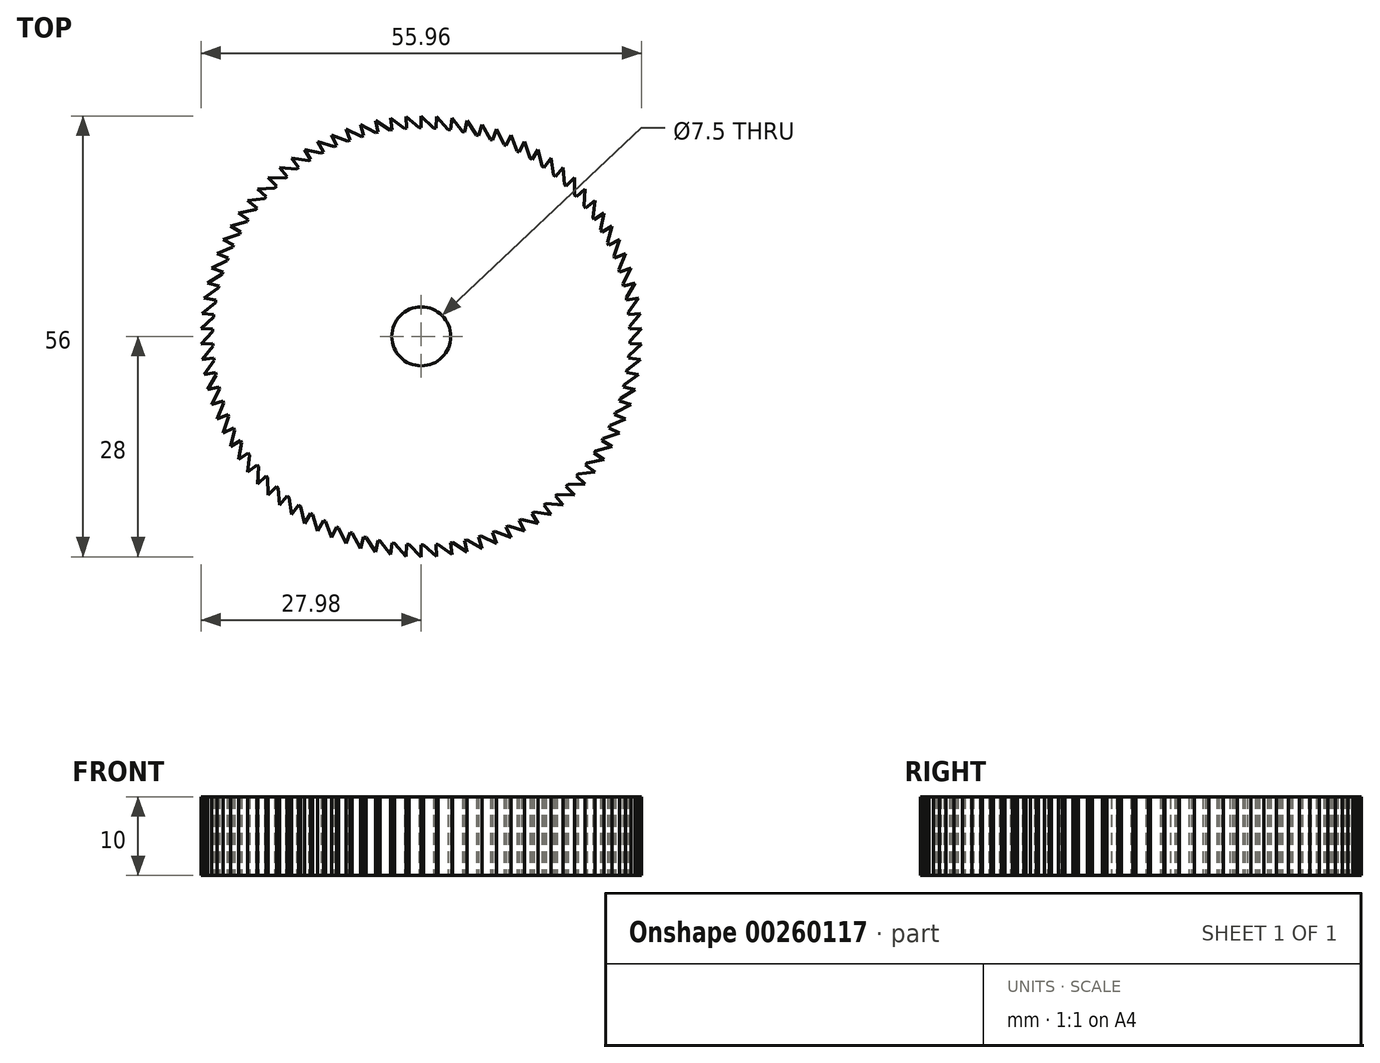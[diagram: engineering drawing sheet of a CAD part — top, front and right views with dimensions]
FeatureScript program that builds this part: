
annotation { "Feature Type Name" : "Feature", "Feature Type Description" : "" }
export const myFeature = defineFeature(function(context is Context, id is Id, definition is map)
    precondition{}
    {
        {
            var Q0;
            Q0=qCreatedBy(makeId("Top.planeOp"),FACE);
            var sketch = newSketch(context, id + "F0", { "sketchPlane" : qUnion([Q0])});
            skArc(sketch, "E0", {"start": v(25.78, -6.12) * mm, "mid": v(26.12, -4.45) * mm, "end": v(26.35, -2.77) * mm, "construction": true});
            skCircle(sketch, "E1", {"center": v(0, 0) * mm, "radius": 3.75 * mm});
            skLineSegment(sketch, "E2", {"start": v(0, 26.5) * mm, "end": v(0, 28) * mm});
            skLineSegment(sketch, "E3", {"start": v(0, 28) * mm, "end": v(1.55, 26.45) * mm});
            skLineSegment(sketch, "E4.anchor1", {"start": v(0, 0) * mm, "end": v(0, 26.5) * mm, "construction": true});
            skLineSegment(sketch, "E4.anchor2", {"start": v(0, 0) * mm, "end": v(0, 26.5) * mm, "construction": true});
            skLineSegment(sketch, "E5.1.0", {"start": v(-1.95, 27.93) * mm, "end": v(-0.3, 26.5) * mm});
            skLineSegment(sketch, "E5.1.1", {"start": v(-1.85, 26.44) * mm, "end": v(-1.95, 27.93) * mm});
            skLineSegment(sketch, "E5.2.0", {"start": v(-3.9, 27.73) * mm, "end": v(-2.15, 26.41) * mm});
            skLineSegment(sketch, "E5.2.1", {"start": v(-3.69, 26.24) * mm, "end": v(-3.9, 27.73) * mm});
            skLineSegment(sketch, "E5.3.0", {"start": v(-5.82, 27.39) * mm, "end": v(-3.99, 26.2) * mm});
            skLineSegment(sketch, "E5.3.1", {"start": v(-5.5, 25.92) * mm, "end": v(-5.82, 27.39) * mm});
            skLineSegment(sketch, "E5.4.0", {"start": v(-7.72, 26.92) * mm, "end": v(-5.8, 25.86) * mm});
            skLineSegment(sketch, "E5.4.1", {"start": v(-7.3, 25.47) * mm, "end": v(-7.72, 26.92) * mm});
            skLineSegment(sketch, "E5.5.0", {"start": v(-9.58, 26.31) * mm, "end": v(-7.6, 25.39) * mm});
            skLineSegment(sketch, "E5.5.1", {"start": v(-9.06, 24.9) * mm, "end": v(-9.58, 26.31) * mm});
            skLineSegment(sketch, "E5.6.0", {"start": v(-11.39, 25.58) * mm, "end": v(-9.35, 24.8) * mm});
            skLineSegment(sketch, "E5.6.1", {"start": v(-10.78, 24.2) * mm, "end": v(-11.39, 25.58) * mm});
            skLineSegment(sketch, "E5.7.0", {"start": v(-13.15, 24.72) * mm, "end": v(-11.06, 24.08) * mm});
            skLineSegment(sketch, "E5.7.1", {"start": v(-12.44, 23.4) * mm, "end": v(-13.15, 24.72) * mm});
            skLineSegment(sketch, "E5.8.0", {"start": v(-14.84, 23.75) * mm, "end": v(-12.7, 23.25) * mm});
            skLineSegment(sketch, "E5.8.1", {"start": v(-14.04, 22.47) * mm, "end": v(-14.84, 23.75) * mm});
            skLineSegment(sketch, "E5.9.0", {"start": v(-16.46, 22.65) * mm, "end": v(-14.3, 22.31) * mm});
            skLineSegment(sketch, "E5.9.1", {"start": v(-15.58, 21.44) * mm, "end": v(-16.46, 22.65) * mm});
            skLineSegment(sketch, "E5.10.0", {"start": v(-18, 21.45) * mm, "end": v(-15.82, 21.26) * mm});
            skLineSegment(sketch, "E5.10.1", {"start": v(-17.03, 20.3) * mm, "end": v(-18, 21.45) * mm});
            skLineSegment(sketch, "E5.11.0", {"start": v(-19.45, 20.14) * mm, "end": v(-17.27, 20.1) * mm});
            skLineSegment(sketch, "E5.11.1", {"start": v(-18.4, 19.06) * mm, "end": v(-19.45, 20.14) * mm});
            skLineSegment(sketch, "E5.12.0", {"start": v(-20.8, 18.74) * mm, "end": v(-18.63, 18.85) * mm});
            skLineSegment(sketch, "E5.12.1", {"start": v(-19.7, 17.73) * mm, "end": v(-20.8, 18.74) * mm});
            skLineSegment(sketch, "E5.13.0", {"start": v(-22.06, 17.24) * mm, "end": v(-19.9, 17.5) * mm});
            skLineSegment(sketch, "E5.13.1", {"start": v(-20.88, 16.32) * mm, "end": v(-22.06, 17.24) * mm});
            skLineSegment(sketch, "E5.14.0", {"start": v(-23.21, 15.66) * mm, "end": v(-21.07, 16.07) * mm});
            skLineSegment(sketch, "E5.14.1", {"start": v(-21.97, 14.82) * mm, "end": v(-23.21, 15.66) * mm});
            skLineSegment(sketch, "E5.15.0", {"start": v(-24.25, 14) * mm, "end": v(-22.14, 14.57) * mm});
            skLineSegment(sketch, "E5.15.1", {"start": v(-22.95, 13.25) * mm, "end": v(-24.25, 14) * mm});
            skLineSegment(sketch, "E5.16.0", {"start": v(-25.17, 12.27) * mm, "end": v(-23.1, 12.99) * mm});
            skLineSegment(sketch, "E5.16.1", {"start": v(-23.82, 11.62) * mm, "end": v(-25.17, 12.27) * mm});
            skLineSegment(sketch, "E5.17.0", {"start": v(-25.96, 10.49) * mm, "end": v(-23.95, 11.34) * mm});
            skLineSegment(sketch, "E5.17.1", {"start": v(-24.57, 9.93) * mm, "end": v(-25.96, 10.49) * mm});
            skLineSegment(sketch, "E5.18.0", {"start": v(-26.63, 8.65) * mm, "end": v(-24.68, 9.64) * mm});
            skLineSegment(sketch, "E5.18.1", {"start": v(-25.2, 8.19) * mm, "end": v(-26.63, 8.65) * mm});
            skLineSegment(sketch, "E5.19.0", {"start": v(-27.17, 6.77) * mm, "end": v(-25.3, 7.9) * mm});
            skLineSegment(sketch, "E5.19.1", {"start": v(-25.71, 6.41) * mm, "end": v(-27.17, 6.77) * mm});
            skLineSegment(sketch, "E5.20.0", {"start": v(-27.57, 4.86) * mm, "end": v(-25.78, 6.12) * mm});
            skLineSegment(sketch, "E5.20.1", {"start": v(-26.1, 4.6) * mm, "end": v(-27.57, 4.86) * mm});
            skLineSegment(sketch, "E5.21.0", {"start": v(-27.85, 2.93) * mm, "end": v(-26.15, 4.3) * mm});
            skLineSegment(sketch, "E5.21.1", {"start": v(-26.35, 2.77) * mm, "end": v(-27.85, 2.93) * mm});
            skLineSegment(sketch, "E5.22.0", {"start": v(-27.98, 0.98) * mm, "end": v(-26.38, 2.47) * mm});
            skLineSegment(sketch, "E5.22.1", {"start": v(-26.48, 0.92) * mm, "end": v(-27.98, 0.98) * mm});
            skLineSegment(sketch, "E5.23.0", {"start": v(-27.98, -0.98) * mm, "end": v(-26.5, 0.62) * mm});
            skLineSegment(sketch, "E5.23.1", {"start": v(-26.48, -0.92) * mm, "end": v(-27.98, -0.98) * mm});
            skLineSegment(sketch, "E5.24.0", {"start": v(-27.85, -2.93) * mm, "end": v(-26.47, -1.23) * mm});
            skLineSegment(sketch, "E5.24.1", {"start": v(-26.35, -2.77) * mm, "end": v(-27.85, -2.93) * mm});
            skLineSegment(sketch, "E5.25.0", {"start": v(-27.57, -4.86) * mm, "end": v(-26.32, -3.07) * mm});
            skLineSegment(sketch, "E5.25.1", {"start": v(-26.1, -4.6) * mm, "end": v(-27.57, -4.86) * mm});
            skLineSegment(sketch, "E5.26.0", {"start": v(-27.17, -6.77) * mm, "end": v(-26.04, -4.9) * mm});
            skLineSegment(sketch, "E5.26.1", {"start": v(-25.71, -6.41) * mm, "end": v(-27.17, -6.77) * mm});
            skLineSegment(sketch, "E5.27.0", {"start": v(-26.63, -8.65) * mm, "end": v(-25.64, -6.7) * mm});
            skLineSegment(sketch, "E5.27.1", {"start": v(-25.2, -8.19) * mm, "end": v(-26.63, -8.65) * mm});
            skLineSegment(sketch, "E5.28.0", {"start": v(-25.96, -10.49) * mm, "end": v(-25.1, -8.48) * mm});
            skLineSegment(sketch, "E5.28.1", {"start": v(-24.57, -9.93) * mm, "end": v(-25.96, -10.49) * mm});
            skLineSegment(sketch, "E5.29.0", {"start": v(-25.17, -12.27) * mm, "end": v(-24.45, -10.2) * mm});
            skLineSegment(sketch, "E5.29.1", {"start": v(-23.82, -11.62) * mm, "end": v(-25.17, -12.27) * mm});
            skLineSegment(sketch, "E5.30.0", {"start": v(-24.25, -14) * mm, "end": v(-23.68, -11.89) * mm});
            skLineSegment(sketch, "E5.30.1", {"start": v(-22.95, -13.25) * mm, "end": v(-24.25, -14) * mm});
            skLineSegment(sketch, "E5.31.0", {"start": v(-23.21, -15.66) * mm, "end": v(-22.8, -13.51) * mm});
            skLineSegment(sketch, "E5.31.1", {"start": v(-21.97, -14.82) * mm, "end": v(-23.21, -15.66) * mm});
            skLineSegment(sketch, "E5.32.0", {"start": v(-22.06, -17.24) * mm, "end": v(-21.8, -15.07) * mm});
            skLineSegment(sketch, "E5.32.1", {"start": v(-20.88, -16.32) * mm, "end": v(-22.06, -17.24) * mm});
            skLineSegment(sketch, "E5.33.0", {"start": v(-20.8, -18.74) * mm, "end": v(-20.7, -16.55) * mm});
            skLineSegment(sketch, "E5.33.1", {"start": v(-19.7, -17.73) * mm, "end": v(-20.8, -18.74) * mm});
            skLineSegment(sketch, "E5.34.0", {"start": v(-19.45, -20.14) * mm, "end": v(-19.49, -17.96) * mm});
            skLineSegment(sketch, "E5.34.1", {"start": v(-18.4, -19.06) * mm, "end": v(-19.45, -20.14) * mm});
            skLineSegment(sketch, "E5.35.0", {"start": v(-18, -21.45) * mm, "end": v(-18.19, -19.27) * mm});
            skLineSegment(sketch, "E5.35.1", {"start": v(-17.03, -20.3) * mm, "end": v(-18, -21.45) * mm});
            skLineSegment(sketch, "E5.36.0", {"start": v(-16.46, -22.65) * mm, "end": v(-16.8, -20.5) * mm});
            skLineSegment(sketch, "E5.36.1", {"start": v(-15.58, -21.44) * mm, "end": v(-16.46, -22.65) * mm});
            skLineSegment(sketch, "E5.37.0", {"start": v(-14.84, -23.75) * mm, "end": v(-15.33, -21.62) * mm});
            skLineSegment(sketch, "E5.37.1", {"start": v(-14.04, -22.47) * mm, "end": v(-14.84, -23.75) * mm});
            skLineSegment(sketch, "E5.38.0", {"start": v(-13.15, -24.72) * mm, "end": v(-13.78, -22.63) * mm});
            skLineSegment(sketch, "E5.38.1", {"start": v(-12.44, -23.4) * mm, "end": v(-13.15, -24.72) * mm});
            skLineSegment(sketch, "E5.39.0", {"start": v(-11.39, -25.58) * mm, "end": v(-12.17, -23.54) * mm});
            skLineSegment(sketch, "E5.39.1", {"start": v(-10.78, -24.2) * mm, "end": v(-11.39, -25.58) * mm});
            skLineSegment(sketch, "E5.40.0", {"start": v(-9.58, -26.31) * mm, "end": v(-10.5, -24.33) * mm});
            skLineSegment(sketch, "E5.40.1", {"start": v(-9.06, -24.9) * mm, "end": v(-9.58, -26.31) * mm});
            skLineSegment(sketch, "E5.41.0", {"start": v(-7.72, -26.92) * mm, "end": v(-8.78, -25) * mm});
            skLineSegment(sketch, "E5.41.1", {"start": v(-7.3, -25.47) * mm, "end": v(-7.72, -26.92) * mm});
            skLineSegment(sketch, "E5.42.0", {"start": v(-5.82, -27.39) * mm, "end": v(-7.01, -25.56) * mm});
            skLineSegment(sketch, "E5.42.1", {"start": v(-5.5, -25.92) * mm, "end": v(-5.82, -27.39) * mm});
            skLineSegment(sketch, "E5.43.0", {"start": v(-3.9, -27.73) * mm, "end": v(-5.21, -25.98) * mm});
            skLineSegment(sketch, "E5.43.1", {"start": v(-3.69, -26.24) * mm, "end": v(-3.9, -27.73) * mm});
            skLineSegment(sketch, "E5.44.0", {"start": v(-1.95, -27.93) * mm, "end": v(-3.39, -26.28) * mm});
            skLineSegment(sketch, "E5.44.1", {"start": v(-1.85, -26.44) * mm, "end": v(-1.95, -27.93) * mm});
            skLineSegment(sketch, "E5.45.0", {"start": v(0, -28) * mm, "end": v(-1.55, -26.45) * mm});
            skLineSegment(sketch, "E5.45.1", {"start": v(0, -26.5) * mm, "end": v(0, -28) * mm});
            skLineSegment(sketch, "E5.46.0", {"start": v(1.95, -27.93) * mm, "end": v(0.3, -26.5) * mm});
            skLineSegment(sketch, "E5.46.1", {"start": v(1.85, -26.44) * mm, "end": v(1.95, -27.93) * mm});
            skLineSegment(sketch, "E5.47.0", {"start": v(3.9, -27.73) * mm, "end": v(2.15, -26.41) * mm});
            skLineSegment(sketch, "E5.47.1", {"start": v(3.69, -26.24) * mm, "end": v(3.9, -27.73) * mm});
            skLineSegment(sketch, "E5.48.0", {"start": v(5.82, -27.39) * mm, "end": v(3.99, -26.2) * mm});
            skLineSegment(sketch, "E5.48.1", {"start": v(5.5, -25.92) * mm, "end": v(5.82, -27.39) * mm});
            skLineSegment(sketch, "E5.49.0", {"start": v(7.72, -26.92) * mm, "end": v(5.8, -25.86) * mm});
            skLineSegment(sketch, "E5.49.1", {"start": v(7.3, -25.47) * mm, "end": v(7.72, -26.92) * mm});
            skLineSegment(sketch, "E5.50.0", {"start": v(9.58, -26.31) * mm, "end": v(7.6, -25.39) * mm});
            skLineSegment(sketch, "E5.50.1", {"start": v(9.06, -24.9) * mm, "end": v(9.58, -26.31) * mm});
            skLineSegment(sketch, "E5.51.0", {"start": v(11.39, -25.58) * mm, "end": v(9.35, -24.8) * mm});
            skLineSegment(sketch, "E5.51.1", {"start": v(10.78, -24.2) * mm, "end": v(11.39, -25.58) * mm});
            skLineSegment(sketch, "E5.52.0", {"start": v(13.15, -24.72) * mm, "end": v(11.06, -24.08) * mm});
            skLineSegment(sketch, "E5.52.1", {"start": v(12.44, -23.4) * mm, "end": v(13.15, -24.72) * mm});
            skLineSegment(sketch, "E5.53.0", {"start": v(14.84, -23.75) * mm, "end": v(12.7, -23.25) * mm});
            skLineSegment(sketch, "E5.53.1", {"start": v(14.04, -22.47) * mm, "end": v(14.84, -23.75) * mm});
            skLineSegment(sketch, "E5.54.0", {"start": v(16.46, -22.65) * mm, "end": v(14.3, -22.31) * mm});
            skLineSegment(sketch, "E5.54.1", {"start": v(15.58, -21.44) * mm, "end": v(16.46, -22.65) * mm});
            skLineSegment(sketch, "E5.55.0", {"start": v(18, -21.45) * mm, "end": v(15.82, -21.26) * mm});
            skLineSegment(sketch, "E5.55.1", {"start": v(17.03, -20.3) * mm, "end": v(18, -21.45) * mm});
            skLineSegment(sketch, "E5.56.0", {"start": v(19.45, -20.14) * mm, "end": v(17.27, -20.1) * mm});
            skLineSegment(sketch, "E5.56.1", {"start": v(18.4, -19.06) * mm, "end": v(19.45, -20.14) * mm});
            skLineSegment(sketch, "E5.57.0", {"start": v(20.8, -18.74) * mm, "end": v(18.63, -18.85) * mm});
            skLineSegment(sketch, "E5.57.1", {"start": v(19.7, -17.73) * mm, "end": v(20.8, -18.74) * mm});
            skLineSegment(sketch, "E5.58.0", {"start": v(22.06, -17.24) * mm, "end": v(19.9, -17.5) * mm});
            skLineSegment(sketch, "E5.58.1", {"start": v(20.88, -16.32) * mm, "end": v(22.06, -17.24) * mm});
            skLineSegment(sketch, "E5.59.0", {"start": v(23.21, -15.66) * mm, "end": v(21.07, -16.07) * mm});
            skLineSegment(sketch, "E5.59.1", {"start": v(21.97, -14.82) * mm, "end": v(23.21, -15.66) * mm});
            skLineSegment(sketch, "E5.60.0", {"start": v(24.25, -14) * mm, "end": v(22.14, -14.57) * mm});
            skLineSegment(sketch, "E5.60.1", {"start": v(22.95, -13.25) * mm, "end": v(24.25, -14) * mm});
            skLineSegment(sketch, "E5.61.0", {"start": v(25.17, -12.27) * mm, "end": v(23.1, -12.99) * mm});
            skLineSegment(sketch, "E5.61.1", {"start": v(23.82, -11.62) * mm, "end": v(25.17, -12.27) * mm});
            skLineSegment(sketch, "E5.62.0", {"start": v(25.96, -10.49) * mm, "end": v(23.95, -11.34) * mm});
            skLineSegment(sketch, "E5.62.1", {"start": v(24.57, -9.93) * mm, "end": v(25.96, -10.49) * mm});
            skLineSegment(sketch, "E5.63.0", {"start": v(26.63, -8.65) * mm, "end": v(24.68, -9.64) * mm});
            skLineSegment(sketch, "E5.63.1", {"start": v(25.2, -8.19) * mm, "end": v(26.63, -8.65) * mm});
            skLineSegment(sketch, "E5.64.0", {"start": v(27.17, -6.77) * mm, "end": v(25.3, -7.9) * mm});
            skLineSegment(sketch, "E5.64.1", {"start": v(25.71, -6.41) * mm, "end": v(27.17, -6.77) * mm});
            skLineSegment(sketch, "E5.65.0", {"start": v(27.57, -4.86) * mm, "end": v(25.78, -6.12) * mm});
            skLineSegment(sketch, "E5.65.1", {"start": v(26.1, -4.6) * mm, "end": v(27.57, -4.86) * mm});
            skLineSegment(sketch, "E5.66.0", {"start": v(27.85, -2.93) * mm, "end": v(26.15, -4.3) * mm});
            skLineSegment(sketch, "E5.66.1", {"start": v(26.35, -2.77) * mm, "end": v(27.85, -2.93) * mm});
            skLineSegment(sketch, "E5.67.0", {"start": v(27.98, -0.98) * mm, "end": v(26.38, -2.47) * mm});
            skLineSegment(sketch, "E5.67.1", {"start": v(26.48, -0.92) * mm, "end": v(27.98, -0.98) * mm});
            skLineSegment(sketch, "E5.68.0", {"start": v(27.98, 0.98) * mm, "end": v(26.5, -0.62) * mm});
            skLineSegment(sketch, "E5.68.1", {"start": v(26.48, 0.92) * mm, "end": v(27.98, 0.98) * mm});
            skLineSegment(sketch, "E5.69.0", {"start": v(27.85, 2.93) * mm, "end": v(26.47, 1.23) * mm});
            skLineSegment(sketch, "E5.69.1", {"start": v(26.35, 2.77) * mm, "end": v(27.85, 2.93) * mm});
            skLineSegment(sketch, "E5.70.0", {"start": v(27.57, 4.86) * mm, "end": v(26.32, 3.07) * mm});
            skLineSegment(sketch, "E5.70.1", {"start": v(26.1, 4.6) * mm, "end": v(27.57, 4.86) * mm});
            skLineSegment(sketch, "E5.71.0", {"start": v(27.17, 6.77) * mm, "end": v(26.04, 4.9) * mm});
            skLineSegment(sketch, "E5.71.1", {"start": v(25.71, 6.41) * mm, "end": v(27.17, 6.77) * mm});
            skLineSegment(sketch, "E5.72.0", {"start": v(26.63, 8.65) * mm, "end": v(25.64, 6.7) * mm});
            skLineSegment(sketch, "E5.72.1", {"start": v(25.2, 8.19) * mm, "end": v(26.63, 8.65) * mm});
            skLineSegment(sketch, "E5.73.0", {"start": v(25.96, 10.49) * mm, "end": v(25.1, 8.48) * mm});
            skLineSegment(sketch, "E5.73.1", {"start": v(24.57, 9.93) * mm, "end": v(25.96, 10.49) * mm});
            skLineSegment(sketch, "E5.74.0", {"start": v(25.17, 12.27) * mm, "end": v(24.45, 10.2) * mm});
            skLineSegment(sketch, "E5.74.1", {"start": v(23.82, 11.62) * mm, "end": v(25.17, 12.27) * mm});
            skLineSegment(sketch, "E5.75.0", {"start": v(24.25, 14) * mm, "end": v(23.68, 11.89) * mm});
            skLineSegment(sketch, "E5.75.1", {"start": v(22.95, 13.25) * mm, "end": v(24.25, 14) * mm});
            skLineSegment(sketch, "E5.76.0", {"start": v(23.21, 15.66) * mm, "end": v(22.8, 13.51) * mm});
            skLineSegment(sketch, "E5.76.1", {"start": v(21.97, 14.82) * mm, "end": v(23.21, 15.66) * mm});
            skLineSegment(sketch, "E5.77.0", {"start": v(22.06, 17.24) * mm, "end": v(21.8, 15.07) * mm});
            skLineSegment(sketch, "E5.77.1", {"start": v(20.88, 16.32) * mm, "end": v(22.06, 17.24) * mm});
            skLineSegment(sketch, "E5.78.0", {"start": v(20.8, 18.74) * mm, "end": v(20.7, 16.55) * mm});
            skLineSegment(sketch, "E5.78.1", {"start": v(19.7, 17.73) * mm, "end": v(20.8, 18.74) * mm});
            skLineSegment(sketch, "E5.79.0", {"start": v(19.45, 20.14) * mm, "end": v(19.49, 17.96) * mm});
            skLineSegment(sketch, "E5.79.1", {"start": v(18.4, 19.06) * mm, "end": v(19.45, 20.14) * mm});
            skLineSegment(sketch, "E5.80.0", {"start": v(18, 21.45) * mm, "end": v(18.19, 19.27) * mm});
            skLineSegment(sketch, "E5.80.1", {"start": v(17.03, 20.3) * mm, "end": v(18, 21.45) * mm});
            skLineSegment(sketch, "E5.81.0", {"start": v(16.46, 22.65) * mm, "end": v(16.8, 20.5) * mm});
            skLineSegment(sketch, "E5.81.1", {"start": v(15.58, 21.44) * mm, "end": v(16.46, 22.65) * mm});
            skLineSegment(sketch, "E5.82.0", {"start": v(14.84, 23.75) * mm, "end": v(15.33, 21.62) * mm});
            skLineSegment(sketch, "E5.82.1", {"start": v(14.04, 22.47) * mm, "end": v(14.84, 23.75) * mm});
            skLineSegment(sketch, "E5.83.0", {"start": v(13.15, 24.72) * mm, "end": v(13.78, 22.63) * mm});
            skLineSegment(sketch, "E5.83.1", {"start": v(12.44, 23.4) * mm, "end": v(13.15, 24.72) * mm});
            skLineSegment(sketch, "E5.84.0", {"start": v(11.39, 25.58) * mm, "end": v(12.17, 23.54) * mm});
            skLineSegment(sketch, "E5.84.1", {"start": v(10.78, 24.2) * mm, "end": v(11.39, 25.58) * mm});
            skLineSegment(sketch, "E5.85.0", {"start": v(9.58, 26.31) * mm, "end": v(10.5, 24.33) * mm});
            skLineSegment(sketch, "E5.85.1", {"start": v(9.06, 24.9) * mm, "end": v(9.58, 26.31) * mm});
            skLineSegment(sketch, "E5.86.0", {"start": v(7.72, 26.92) * mm, "end": v(8.78, 25) * mm});
            skLineSegment(sketch, "E5.86.1", {"start": v(7.3, 25.47) * mm, "end": v(7.72, 26.92) * mm});
            skLineSegment(sketch, "E5.87.0", {"start": v(5.82, 27.39) * mm, "end": v(7.01, 25.56) * mm});
            skLineSegment(sketch, "E5.87.1", {"start": v(5.5, 25.92) * mm, "end": v(5.82, 27.39) * mm});
            skLineSegment(sketch, "E5.88.0", {"start": v(3.9, 27.73) * mm, "end": v(5.21, 25.98) * mm});
            skLineSegment(sketch, "E5.88.1", {"start": v(3.69, 26.24) * mm, "end": v(3.9, 27.73) * mm});
            skLineSegment(sketch, "E5.89.0", {"start": v(1.95, 27.93) * mm, "end": v(3.39, 26.28) * mm});
            skLineSegment(sketch, "E5.89.1", {"start": v(1.85, 26.44) * mm, "end": v(1.95, 27.93) * mm});
            skArc(sketch, "E6.trimOffspring", {"start": v(26.48, -0.92) * mm, "mid": v(-26.26, 3.54) * mm, "end": v(25.78, -6.12) * mm, "construction": true});
            skLineSegment(sketch, "E7", {"start": v(26.35, -2.77) * mm, "end": v(26.38, -2.47) * mm});
            skLineSegment(sketch, "E8.1.0", {"start": v(26.48, -0.92) * mm, "end": v(26.5, -0.62) * mm});
            skLineSegment(sketch, "E8.2.0", {"start": v(26.48, 0.92) * mm, "end": v(26.47, 1.23) * mm});
            skLineSegment(sketch, "E8.3.0", {"start": v(26.35, 2.77) * mm, "end": v(26.32, 3.07) * mm});
            skLineSegment(sketch, "E8.4.0", {"start": v(26.1, 4.6) * mm, "end": v(26.04, 4.9) * mm});
            skLineSegment(sketch, "E8.5.0", {"start": v(25.71, 6.41) * mm, "end": v(25.64, 6.7) * mm});
            skLineSegment(sketch, "E8.6.0", {"start": v(25.2, 8.19) * mm, "end": v(25.1, 8.48) * mm});
            skLineSegment(sketch, "E8.7.0", {"start": v(24.57, 9.93) * mm, "end": v(24.45, 10.2) * mm});
            skLineSegment(sketch, "E8.8.0", {"start": v(23.82, 11.62) * mm, "end": v(23.68, 11.89) * mm});
            skLineSegment(sketch, "E8.9.0", {"start": v(22.95, 13.25) * mm, "end": v(22.8, 13.51) * mm});
            skLineSegment(sketch, "E8.10.0", {"start": v(21.97, 14.82) * mm, "end": v(21.8, 15.07) * mm});
            skLineSegment(sketch, "E8.11.0", {"start": v(20.88, 16.32) * mm, "end": v(20.7, 16.55) * mm});
            skLineSegment(sketch, "E8.12.0", {"start": v(19.7, 17.73) * mm, "end": v(19.49, 17.96) * mm});
            skLineSegment(sketch, "E8.13.0", {"start": v(18.4, 19.06) * mm, "end": v(18.19, 19.27) * mm});
            skLineSegment(sketch, "E8.14.0", {"start": v(17.03, 20.3) * mm, "end": v(16.8, 20.5) * mm});
            skLineSegment(sketch, "E8.15.0", {"start": v(15.58, 21.44) * mm, "end": v(15.33, 21.62) * mm});
            skLineSegment(sketch, "E8.16.0", {"start": v(14.04, 22.47) * mm, "end": v(13.78, 22.63) * mm});
            skLineSegment(sketch, "E8.17.0", {"start": v(12.44, 23.4) * mm, "end": v(12.17, 23.54) * mm});
            skLineSegment(sketch, "E8.18.0", {"start": v(10.78, 24.2) * mm, "end": v(10.5, 24.33) * mm});
            skLineSegment(sketch, "E8.19.0", {"start": v(9.06, 24.9) * mm, "end": v(8.78, 25) * mm});
            skLineSegment(sketch, "E8.20.0", {"start": v(7.3, 25.47) * mm, "end": v(7.01, 25.56) * mm});
            skLineSegment(sketch, "E8.21.0", {"start": v(5.5, 25.92) * mm, "end": v(5.21, 25.98) * mm});
            skLineSegment(sketch, "E8.22.0", {"start": v(3.69, 26.24) * mm, "end": v(3.39, 26.28) * mm});
            skLineSegment(sketch, "E8.23.0", {"start": v(1.85, 26.44) * mm, "end": v(1.55, 26.45) * mm});
            skLineSegment(sketch, "E8.24.0", {"start": v(0, 26.5) * mm, "end": v(-0.3, 26.5) * mm});
            skLineSegment(sketch, "E8.25.0", {"start": v(-1.85, 26.44) * mm, "end": v(-2.15, 26.41) * mm});
            skLineSegment(sketch, "E8.26.0", {"start": v(-3.69, 26.24) * mm, "end": v(-3.99, 26.2) * mm});
            skLineSegment(sketch, "E8.27.0", {"start": v(-5.5, 25.92) * mm, "end": v(-5.8, 25.86) * mm});
            skLineSegment(sketch, "E8.28.0", {"start": v(-7.3, 25.47) * mm, "end": v(-7.6, 25.39) * mm});
            skLineSegment(sketch, "E8.29.0", {"start": v(-9.06, 24.9) * mm, "end": v(-9.35, 24.8) * mm});
            skLineSegment(sketch, "E8.30.0", {"start": v(-10.78, 24.2) * mm, "end": v(-11.06, 24.08) * mm});
            skLineSegment(sketch, "E8.31.0", {"start": v(-12.44, 23.4) * mm, "end": v(-12.7, 23.25) * mm});
            skLineSegment(sketch, "E8.32.0", {"start": v(-14.04, 22.47) * mm, "end": v(-14.3, 22.31) * mm});
            skLineSegment(sketch, "E8.33.0", {"start": v(-15.58, 21.44) * mm, "end": v(-15.82, 21.26) * mm});
            skLineSegment(sketch, "E8.34.0", {"start": v(-17.03, 20.3) * mm, "end": v(-17.27, 20.1) * mm});
            skLineSegment(sketch, "E8.35.0", {"start": v(-18.4, 19.06) * mm, "end": v(-18.63, 18.85) * mm});
            skLineSegment(sketch, "E8.36.0", {"start": v(-19.7, 17.73) * mm, "end": v(-19.9, 17.5) * mm});
            skLineSegment(sketch, "E8.37.0", {"start": v(-20.88, 16.32) * mm, "end": v(-21.07, 16.07) * mm});
            skLineSegment(sketch, "E8.38.0", {"start": v(-21.97, 14.82) * mm, "end": v(-22.14, 14.57) * mm});
            skLineSegment(sketch, "E8.39.0", {"start": v(-22.95, 13.25) * mm, "end": v(-23.1, 12.99) * mm});
            skLineSegment(sketch, "E8.40.0", {"start": v(-23.82, 11.62) * mm, "end": v(-23.95, 11.34) * mm});
            skLineSegment(sketch, "E8.41.0", {"start": v(-24.57, 9.93) * mm, "end": v(-24.68, 9.64) * mm});
            skLineSegment(sketch, "E8.42.0", {"start": v(-25.2, 8.19) * mm, "end": v(-25.3, 7.9) * mm});
            skLineSegment(sketch, "E8.43.0", {"start": v(-25.71, 6.41) * mm, "end": v(-25.78, 6.12) * mm});
            skLineSegment(sketch, "E8.44.0", {"start": v(-26.1, 4.6) * mm, "end": v(-26.15, 4.3) * mm});
            skLineSegment(sketch, "E8.45.0", {"start": v(-26.35, 2.77) * mm, "end": v(-26.38, 2.47) * mm});
            skLineSegment(sketch, "E8.46.0", {"start": v(-26.48, 0.92) * mm, "end": v(-26.5, 0.62) * mm});
            skLineSegment(sketch, "E8.47.0", {"start": v(-26.48, -0.92) * mm, "end": v(-26.47, -1.23) * mm});
            skLineSegment(sketch, "E8.48.0", {"start": v(-26.35, -2.77) * mm, "end": v(-26.32, -3.07) * mm});
            skLineSegment(sketch, "E8.49.0", {"start": v(-26.1, -4.6) * mm, "end": v(-26.04, -4.9) * mm});
            skLineSegment(sketch, "E8.50.0", {"start": v(-25.71, -6.41) * mm, "end": v(-25.64, -6.7) * mm});
            skLineSegment(sketch, "E8.51.0", {"start": v(-25.2, -8.19) * mm, "end": v(-25.1, -8.48) * mm});
            skLineSegment(sketch, "E8.52.0", {"start": v(-24.57, -9.93) * mm, "end": v(-24.45, -10.2) * mm});
            skLineSegment(sketch, "E8.53.0", {"start": v(-23.82, -11.62) * mm, "end": v(-23.68, -11.89) * mm});
            skLineSegment(sketch, "E8.54.0", {"start": v(-22.95, -13.25) * mm, "end": v(-22.8, -13.51) * mm});
            skLineSegment(sketch, "E8.55.0", {"start": v(-21.97, -14.82) * mm, "end": v(-21.8, -15.07) * mm});
            skLineSegment(sketch, "E8.56.0", {"start": v(-20.88, -16.32) * mm, "end": v(-20.7, -16.55) * mm});
            skLineSegment(sketch, "E8.57.0", {"start": v(-19.7, -17.73) * mm, "end": v(-19.49, -17.96) * mm});
            skLineSegment(sketch, "E8.58.0", {"start": v(-18.4, -19.06) * mm, "end": v(-18.19, -19.27) * mm});
            skLineSegment(sketch, "E8.59.0", {"start": v(-17.03, -20.3) * mm, "end": v(-16.8, -20.5) * mm});
            skLineSegment(sketch, "E8.60.0", {"start": v(-15.58, -21.44) * mm, "end": v(-15.33, -21.62) * mm});
            skLineSegment(sketch, "E8.61.0", {"start": v(-14.04, -22.47) * mm, "end": v(-13.78, -22.63) * mm});
            skLineSegment(sketch, "E8.62.0", {"start": v(-12.44, -23.4) * mm, "end": v(-12.17, -23.54) * mm});
            skLineSegment(sketch, "E8.63.0", {"start": v(-10.78, -24.2) * mm, "end": v(-10.5, -24.33) * mm});
            skLineSegment(sketch, "E8.64.0", {"start": v(-9.06, -24.9) * mm, "end": v(-8.78, -25) * mm});
            skLineSegment(sketch, "E8.65.0", {"start": v(-7.3, -25.47) * mm, "end": v(-7.01, -25.56) * mm});
            skLineSegment(sketch, "E8.66.0", {"start": v(-5.5, -25.92) * mm, "end": v(-5.21, -25.98) * mm});
            skLineSegment(sketch, "E8.67.0", {"start": v(-3.69, -26.24) * mm, "end": v(-3.39, -26.28) * mm});
            skLineSegment(sketch, "E8.68.0", {"start": v(-1.85, -26.44) * mm, "end": v(-1.55, -26.45) * mm});
            skLineSegment(sketch, "E8.69.0", {"start": v(0, -26.5) * mm, "end": v(0.3, -26.5) * mm});
            skLineSegment(sketch, "E8.70.0", {"start": v(1.85, -26.44) * mm, "end": v(2.15, -26.41) * mm});
            skLineSegment(sketch, "E8.71.0", {"start": v(3.69, -26.24) * mm, "end": v(3.99, -26.2) * mm});
            skLineSegment(sketch, "E8.72.0", {"start": v(5.5, -25.92) * mm, "end": v(5.8, -25.86) * mm});
            skLineSegment(sketch, "E8.73.0", {"start": v(7.3, -25.47) * mm, "end": v(7.6, -25.39) * mm});
            skLineSegment(sketch, "E8.74.0", {"start": v(9.06, -24.9) * mm, "end": v(9.35, -24.8) * mm});
            skLineSegment(sketch, "E8.75.0", {"start": v(10.78, -24.2) * mm, "end": v(11.06, -24.08) * mm});
            skLineSegment(sketch, "E8.76.0", {"start": v(12.44, -23.4) * mm, "end": v(12.7, -23.25) * mm});
            skLineSegment(sketch, "E8.77.0", {"start": v(14.04, -22.47) * mm, "end": v(14.3, -22.31) * mm});
            skLineSegment(sketch, "E8.78.0", {"start": v(15.58, -21.44) * mm, "end": v(15.82, -21.26) * mm});
            skLineSegment(sketch, "E8.79.0", {"start": v(17.03, -20.3) * mm, "end": v(17.27, -20.1) * mm});
            skLineSegment(sketch, "E8.80.0", {"start": v(18.4, -19.06) * mm, "end": v(18.63, -18.85) * mm});
            skLineSegment(sketch, "E8.81.0", {"start": v(19.7, -17.73) * mm, "end": v(19.9, -17.5) * mm});
            skLineSegment(sketch, "E8.82.0", {"start": v(20.88, -16.32) * mm, "end": v(21.07, -16.07) * mm});
            skLineSegment(sketch, "E8.83.0", {"start": v(21.97, -14.82) * mm, "end": v(22.14, -14.57) * mm});
            skLineSegment(sketch, "E8.84.0", {"start": v(22.95, -13.25) * mm, "end": v(23.1, -12.99) * mm});
            skLineSegment(sketch, "E8.85.0", {"start": v(23.82, -11.62) * mm, "end": v(23.95, -11.34) * mm});
            skLineSegment(sketch, "E8.86.0", {"start": v(24.57, -9.93) * mm, "end": v(24.68, -9.64) * mm});
            skLineSegment(sketch, "E8.87.0", {"start": v(25.2, -8.19) * mm, "end": v(25.3, -7.9) * mm});
            skLineSegment(sketch, "E8.88.0", {"start": v(25.71, -6.41) * mm, "end": v(25.78, -6.12) * mm});
            skLineSegment(sketch, "E8.89.0", {"start": v(26.1, -4.6) * mm, "end": v(26.15, -4.3) * mm});
            skSolve(sketch);
        }
        {
            var Q0;
            Q0 = qSketchRegion(id + "F0", true);
            extrude(context, id + "F1", {"entities" : qUnion([Q0]), "depth" : 10 * mm, "offsetDistance" : 25 * mm});
        }
    });
